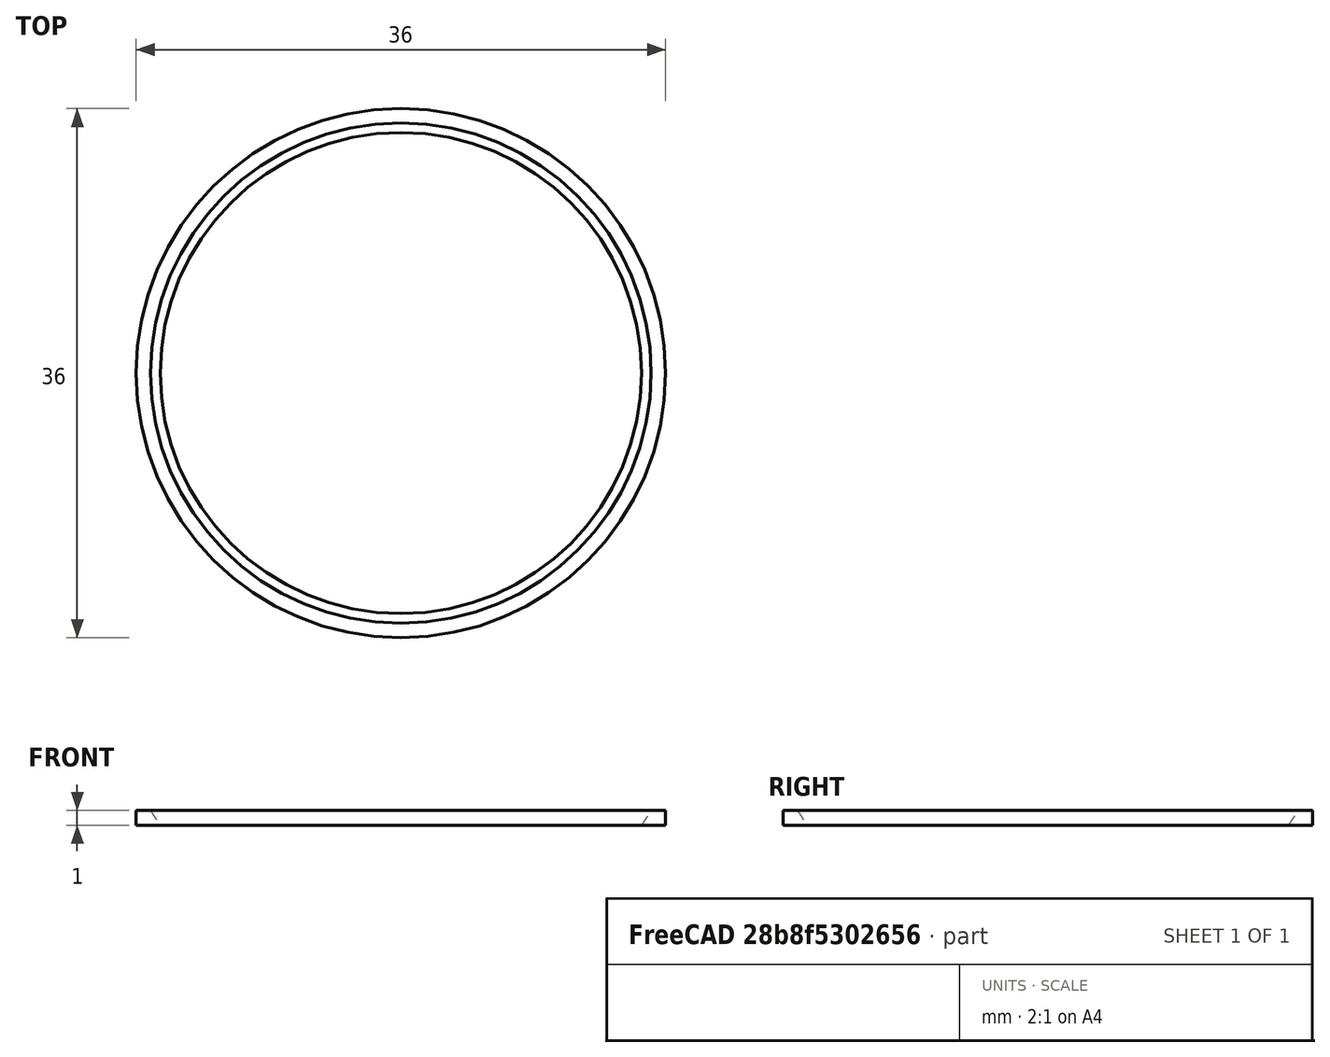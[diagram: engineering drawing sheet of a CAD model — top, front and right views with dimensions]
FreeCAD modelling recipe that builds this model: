
FCSTD DOCUMENT  (FreeCAD 0.20R29603 (Git))
Label: capsule_topper_L1
License: All rights reserved
LicenseURL: http://en.wikipedia.org/wiki/All_rights_reserved
objects: Sketcher::SketchObject×1, PartDesign::Pad×1, PartDesign::Body×1, Part::Sphere×1, Part::Cut×1
note: 6 computed .brp shape members not serialized (recipe doc carries the construction recipe); baked Part::Feature solids carry a one-line shape summary decoded from their .brp

FEATURE [Sketcher::SketchObject] Sketch
  FullyConstrained = true
  MapMode = 5
  Support = -> [XY_Plane]
  sketch-geometry (1):
    g0: Circle CenterX=0 CenterY=0 CenterZ=0 NormalX=0 NormalY=0 NormalZ=1 AngleXU=0 Radius=18
  constraints (2):
    c: Coincident(g0,g-1)
    c: Diameter(g0) = 36
FEATURE [PartDesign::Pad] Pad
  Direction = (0,0,1)
  Length = 1
  Length2 = 10
  Profile = -> Sketch
  ReferenceAxis = -> Sketch [N_Axis]
  Type = 0
FEATURE [PartDesign::Body] Body
  Group = -> [Sketch,Pad]
  Origin = -> Origin
  Tip = -> Pad
FEATURE [Part::Sphere] Sphere  label="Сфера"
  Angle1 = -90
  Angle2 = 90
  Angle3 = 360
  AttacherType = Attacher::AttachEngine3D
  Placement = pos=(0,0,11.5) rot=(0,0,1;0rad)
  Radius = 20
FEATURE [Part::Cut] Cut
  Base = -> Body
  Tool = -> Sphere
